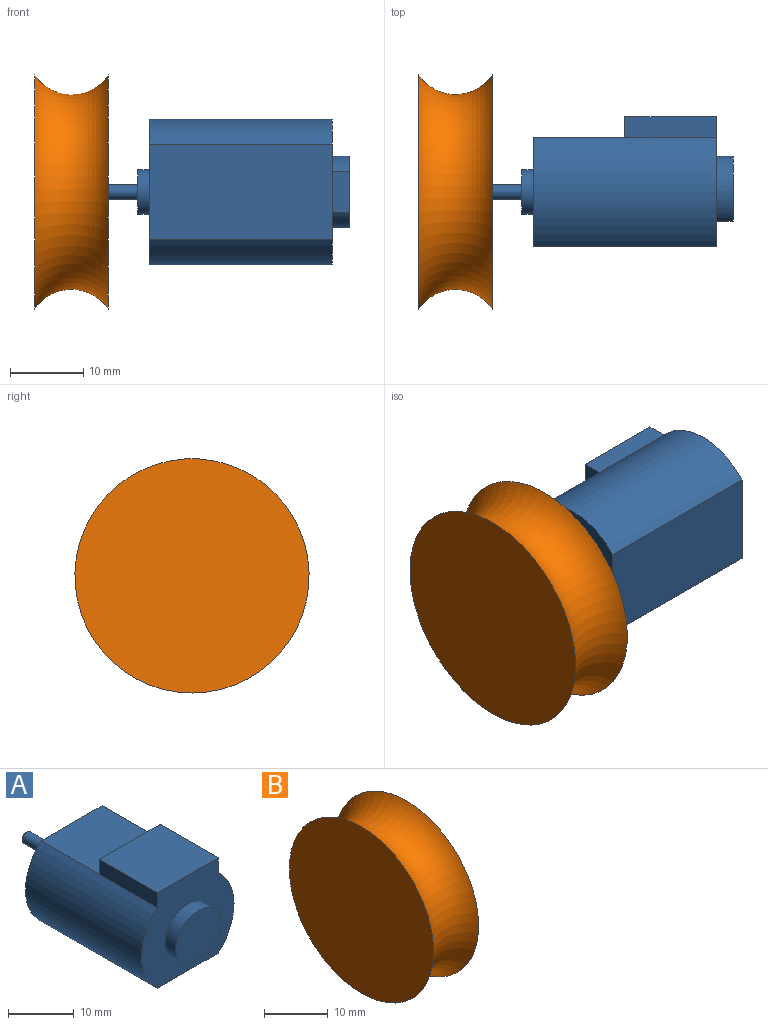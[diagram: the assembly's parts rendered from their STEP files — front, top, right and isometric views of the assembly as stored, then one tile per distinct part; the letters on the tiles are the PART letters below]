
ASSEMBLY  parts=2 mates=1
PART A: 17 faces, bbox 19.9x37x17.8 mm
  f0: plane 19.9x17.78mm, normal (0,-1,0), area 231.6mm2, adj f2,f3,f4,f6,f7,f8,f10,f11
  f1: plane 13.08x12.5mm, normal (0,0,1), area 163.5mm2, adj f3,f4,f5,f9
  f2: plane 25x13.08mm, normal (0,0,-1), area 326.9mm2, adj f0,f3,f4,f5
  f3: cylinder r=9.95mm len=25mm, axis (0,1,0), area 424.8mm2, adj f0,f1,f2,f5,f8
  f4: cylinder r=9.95mm len=25mm, axis (0,1,0), area 424.8mm2, adj f0,f1,f2,f5,f7
  f5: plane 19.9x15mm, normal (0,1,0), area 237.9mm2, adj f1,f2,f3,f4,f13
  f6: plane 13.08x12.5mm, normal (0,0,1), area 163.5mm2, adj f0,f7,f8,f9
  f7: plane 12.5x2.78mm, normal (-1,0,0), area 34.8mm2, adj f0,f4,f6,f9
  f8: plane 12.5x2.78mm, normal (1,0,0), area 34.8mm2, adj f0,f3,f6,f9
  f9: plane 13.08x2.78mm, normal (0,1,0), area 36.4mm2, adj f1,f6,f7,f8
  f10: cylinder r=4.9mm len=9.8mm, axis (0,1,0), area 56.9mm2, adj f0,f11,f12
  f11: plane 5.66x2.3mm, normal (0,0,-1), area 13mm2, adj f0,f10,f12
  f12: plane 9.8x8.9mm, normal (0,-1,0), area 72mm2, adj f10,f11
  f13: cylinder r=3.05mm len=6.1mm, axis (0,-1,0), area 30.7mm2, adj f5,f14
  f14: plane 6.1x6.1mm, normal (0,1,0), area 26.1mm2, adj f13,f15
  f15: cylinder r=1mm len=8.1mm, axis (0,-1,0), area 50.9mm2, adj f14,f16
  f16: plane 2x2mm, normal (0,1,0), area 3.1mm2, adj f15
PART B: 5 faces, bbox 12x41.8x41.8 mm
  f0: plane 2.2x2.2mm, normal (1,0,0), area 3.8mm2, adj f4
  f1: plane 32x32mm, normal (-1,0,0), area 804.2mm2, adj f2
  f2: torus R=19.32mm, axis (1,0,0), area 1057.8mm2, adj f1,f3
  f3: plane 32x32mm, normal (1,0,0), area 800.4mm2, adj f2,f4
  f4: cylinder r=1.1mm len=6mm, axis (1,0,0), area 41.5mm2, adj f0,f3
PLACE A rot(axis=(-0.58,0.58,0.58),120deg) t=(-23.37,-20.44,18.96)mm
PLACE B t=(-42.23,-7.38,-4.84)mm
MATE cylindrical A.f3 <-> B.f2  axis (1,0,0) through (-41.52,-7.38,29.22)mm
